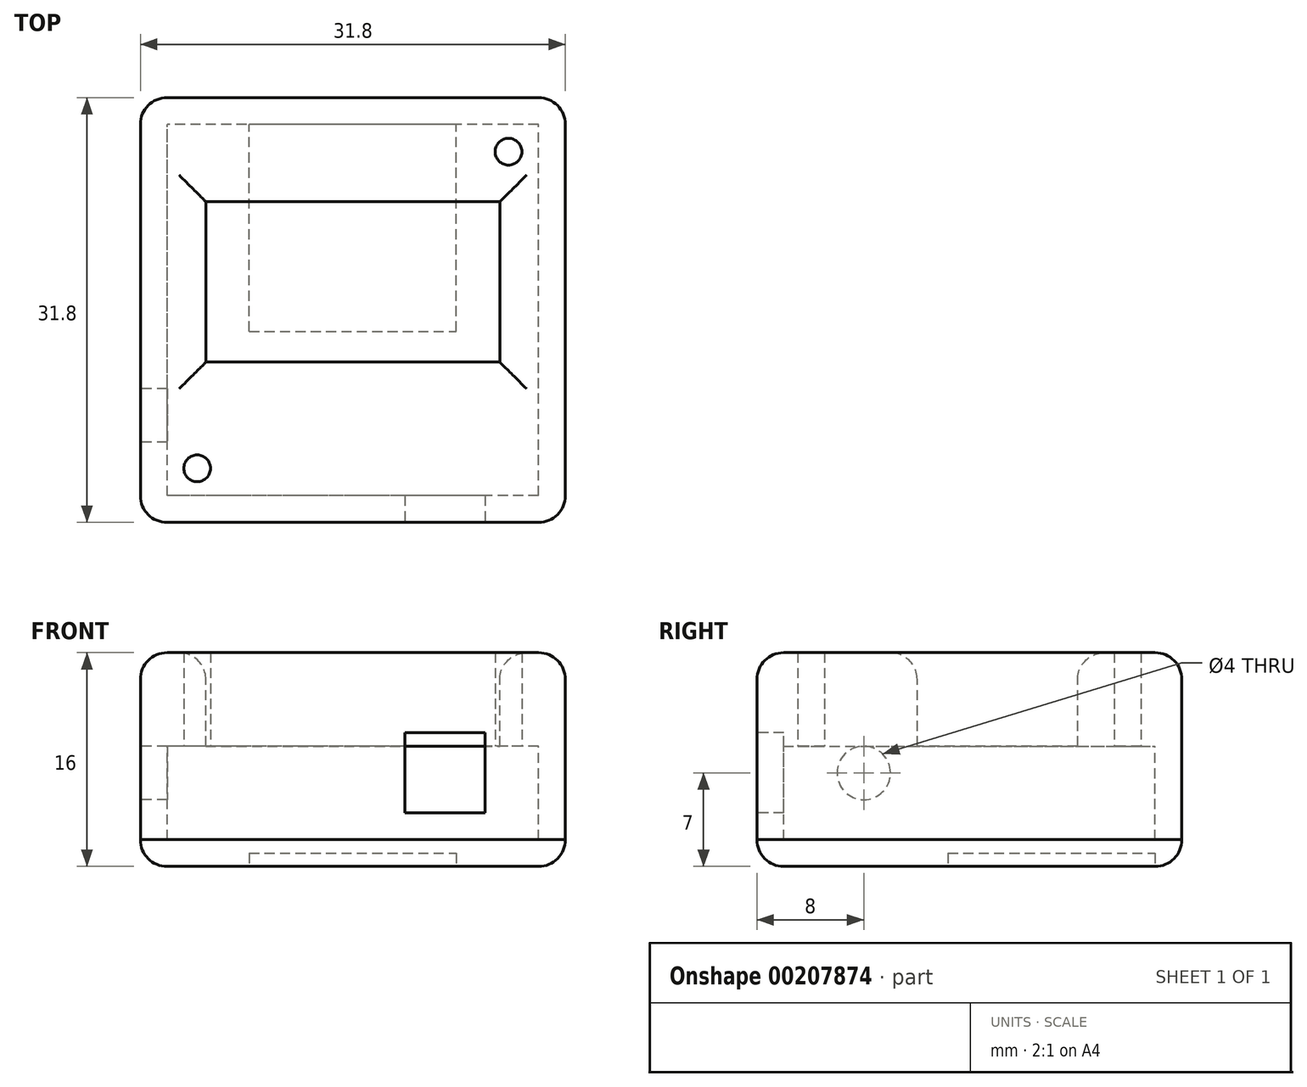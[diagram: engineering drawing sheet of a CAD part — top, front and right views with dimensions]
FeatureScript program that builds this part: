
annotation { "Feature Type Name" : "Feature", "Feature Type Description" : "" }
export const myFeature = defineFeature(function(context is Context, id is Id, definition is map)
    precondition{}
    {
        {
            var Q0;
            Q0=qCreatedBy(makeId("Top.planeOp"),FACE);
            var sketch = newSketch(context, id + "F0", { "sketchPlane" : qUnion([Q0])});
            skLineSegment(sketch, "E0.bottom", {"start": v(13.9, -13.9) * mm, "end": v(-13.9, -13.9) * mm});
            skLineSegment(sketch, "E0.top", {"start": v(13.9, 13.9) * mm, "end": v(-13.9, 13.9) * mm});
            skLineSegment(sketch, "E0.left", {"start": v(13.9, -13.9) * mm, "end": v(13.9, 13.9) * mm});
            skLineSegment(sketch, "E0.right", {"start": v(-13.9, -13.9) * mm, "end": v(-13.9, 13.9) * mm});
            skPoint(sketch, "E0.middle", {"position": v(0, 0) * mm});
            skCircle(sketch, "E1", {"center": v(-11.65, 11.85) * mm, "radius": 1 * mm});
            skLineSegment(sketch, "E2", {"start": v(0, 0) * mm, "end": v(0, 13.9) * mm, "construction": true});
            skCircle(sketch, "E3.MirrorC", {"center": v(11.65, 11.85) * mm, "radius": 1 * mm});
            skLineSegment(sketch, "E4", {"start": v(0, 0) * mm, "end": v(13.9, 0) * mm, "construction": true});
            skCircle(sketch, "E5.MirrorC", {"center": v(-11.65, -11.85) * mm, "radius": 1 * mm});
            skCircle(sketch, "E6.MirrorC", {"center": v(11.65, -11.85) * mm, "radius": 1 * mm});
            skLineSegment(sketch, "E7.bottom", {"start": v(-11, 8.1) * mm, "end": v(11, 8.1) * mm});
            skLineSegment(sketch, "E7.top", {"start": v(-11, -3.9) * mm, "end": v(11, -3.9) * mm});
            skLineSegment(sketch, "E7.left", {"start": v(-11, 8.1) * mm, "end": v(-11, -3.9) * mm});
            skLineSegment(sketch, "E7.right", {"start": v(11, 8.1) * mm, "end": v(11, -3.9) * mm});
            skPoint(sketch, "E8", {"position": v(0, 8.1) * mm});
            skLineSegment(sketch, "E9.0", {"start": v(15.9, -13.9) * mm, "end": v(15.9, 13.9) * mm});
            skLineSegment(sketch, "E9.1", {"start": v(13.9, -15.9) * mm, "end": v(-13.9, -15.9) * mm});
            skLineSegment(sketch, "E9.2", {"start": v(-15.9, -13.9) * mm, "end": v(-15.9, 13.9) * mm});
            skLineSegment(sketch, "E9.3", {"start": v(13.9, 15.9) * mm, "end": v(-13.9, 15.9) * mm});
            skPoint(sketch, "E10.visualSharp", {"position": v(-15.9, 15.9) * mm});
            skArc(sketch, "E10.filletArc", {"start": v(-13.9, 15.9) * mm, "mid": v(-15.31, 15.31) * mm, "end": v(-15.9, 13.9) * mm});
            skPoint(sketch, "E11.visualSharp", {"position": v(15.9, 15.9) * mm});
            skArc(sketch, "E11.filletArc", {"start": v(15.9, 13.9) * mm, "mid": v(15.31, 15.31) * mm, "end": v(13.9, 15.9) * mm});
            skPoint(sketch, "E12.visualSharp", {"position": v(15.9, -15.9) * mm});
            skArc(sketch, "E12.filletArc", {"start": v(13.9, -15.9) * mm, "mid": v(15.31, -15.31) * mm, "end": v(15.9, -13.9) * mm});
            skPoint(sketch, "E13.visualSharp", {"position": v(-15.9, -15.9) * mm});
            skArc(sketch, "E13.filletArc", {"start": v(-15.9, -13.9) * mm, "mid": v(-15.31, -15.31) * mm, "end": v(-13.9, -15.9) * mm});
            skSolve(sketch);
        }
        {
            var Q0;
            Q0=makeQuery(id+"F0.imprint","IMPRINT",FACE,{"disambiguationData":[TD([[makeQuery(id+"F0.imprint","IMPRINT",EDGE,{"derivedFrom":sQuery(id+"F0.wireOp",EDGE,"E0.bottom")}),1.0]])]});
            var Q1;
            Q1=makeQuery(id+"F0.imprint","IMPRINT",FACE,{"disambiguationData":[TD([[makeQuery(id+"F0.imprint","IMPRINT",EDGE,{"derivedFrom":sQuery(id+"F0.wireOp",EDGE,"E0.bottom")}),-1.0]])]});
            var Q2;
            Q2=makeQuery(id+"F0.imprint","IMPRINT",FACE,{"disambiguationData":[TD([[makeQuery(id+"F0.imprint","IMPRINT",EDGE,{"derivedFrom":sQuery(id+"F0.wireOp",EDGE,"E5.MirrorC")}),-1.0]])]});
            var Q3;
            Q3=makeQuery(id+"F0.imprint","IMPRINT",FACE,{"disambiguationData":[TD([[makeQuery(id+"F0.imprint","IMPRINT",EDGE,{"derivedFrom":sQuery(id+"F0.wireOp",EDGE,"E6.MirrorC")}),1.0]])]});
            var Q4;
            Q4=makeQuery(id+"F0.imprint","IMPRINT",FACE,{"disambiguationData":[TD([[makeQuery(id+"F0.imprint","IMPRINT",EDGE,{"derivedFrom":sQuery(id+"F0.wireOp",EDGE,"E3.MirrorC")}),-1.0]])]});
            var Q5;
            Q5=makeQuery(id+"F0.imprint","IMPRINT",FACE,{"disambiguationData":[TD([[makeQuery(id+"F0.imprint","IMPRINT",EDGE,{"derivedFrom":sQuery(id+"F0.wireOp",EDGE,"E1")}),1.0]])]});
            extrude(context, id + "F1", {"entities" : qUnion([Q0, Q1, Q2, Q3, Q4, Q5]), "depth" : 2 * mm});
        }
        {
            var Q0;
            Q0=makeQuery(id+"F1.opExtrude","CAP_EDGE",EDGE,{"disambiguationData":[OSD([sQuery(id+"F0.wireOp",EDGE,"E7.bottom")])],"isStart":false});
            var Q1;
            Q1=makeQuery(id+"F1.opExtrude","CAP_EDGE",EDGE,{"disambiguationData":[OSD([sQuery(id+"F0.wireOp",EDGE,"E7.left")])],"isStart":false});
            var Q2;
            Q2=makeQuery(id+"F1.opExtrude","CAP_EDGE",EDGE,{"disambiguationData":[OSD([sQuery(id+"F0.wireOp",EDGE,"E7.right")])],"isStart":false});
            var Q3;
            Q3=makeQuery(id+"F1.opExtrude","CAP_EDGE",EDGE,{"disambiguationData":[OSD([sQuery(id+"F0.wireOp",EDGE,"E7.top")])],"isStart":false});
            var Q4;
            Q4=makeQuery(id+"F1.opExtrude","CAP_EDGE",EDGE,{"disambiguationData":[OSD([sQuery(id+"F0.wireOp",EDGE,"E9.2")])],"isStart":false});
            fillet(context, id + "F2", {"entities" : qUnion([Q0, Q1, Q2, Q3, Q4]), "radius" : 2 * mm, "tangentPropagation" : true, "allowEdgeOverflow" : false});
        }
        {
            var Q0;
            Q0=makeQuery(id+"F0.imprint","IMPRINT",FACE,{"disambiguationData":[TD([[makeQuery(id+"F0.imprint","IMPRINT",EDGE,{"derivedFrom":sQuery(id+"F0.wireOp",EDGE,"E0.bottom")}),1.0]])]});
            extrude(context, id + "F3", {"entities" : qUnion([Q0]), "operationType" : NewBodyOperationType.ADD, "oppositeDirection" : true, "depth" : 12 * mm});
        }
        {
            var Q0;
            Q0=makeQuery(id+"F3.opExtrude","CAP_FACE",FACE,{"disambiguationData":[OSD([sQuery(id+"F0.wireOp",EDGE,"E0.bottom"),sQuery(id+"F0.wireOp",EDGE,"E0.top"),sQuery(id+"F0.wireOp",EDGE,"E0.left"),sQuery(id+"F0.wireOp",EDGE,"E0.right"),sQuery(id+"F0.wireOp",EDGE,"E9.0"),sQuery(id+"F0.wireOp",EDGE,"E9.1"),sQuery(id+"F0.wireOp",EDGE,"E9.2"),sQuery(id+"F0.wireOp",EDGE,"E9.3"),sQuery(id+"F0.wireOp",EDGE,"E10.filletArc"),sQuery(id+"F0.wireOp",EDGE,"E11.filletArc"),sQuery(id+"F0.wireOp",EDGE,"E12.filletArc"),sQuery(id+"F0.wireOp",EDGE,"E13.filletArc")])],"isStart":false});
            var sketch = newSketch(context, id + "F4", { "sketchPlane" : qUnion([Q0])});
            skLineSegment(sketch, "E14.0", {"start": v(-15.9, 13.9) * mm, "end": v(-15.9, -13.9) * mm});
            skArc(sketch, "E15.0", {"start": v(-15.9, 13.9) * mm, "mid": v(-15.31, 15.31) * mm, "end": v(-13.9, 15.9) * mm});
            skLineSegment(sketch, "E16.0", {"start": v(13.9, 15.9) * mm, "end": v(-13.9, 15.9) * mm});
            skArc(sketch, "E17.0", {"start": v(13.9, 15.9) * mm, "mid": v(15.31, 15.31) * mm, "end": v(15.9, 13.9) * mm});
            skLineSegment(sketch, "E18.0", {"start": v(15.9, 13.9) * mm, "end": v(15.9, -13.9) * mm});
            skArc(sketch, "E19.0", {"start": v(15.9, -13.9) * mm, "mid": v(15.31, -15.31) * mm, "end": v(13.9, -15.9) * mm});
            skLineSegment(sketch, "E20.0", {"start": v(13.9, -15.9) * mm, "end": v(-13.9, -15.9) * mm});
            skArc(sketch, "E21.0", {"start": v(-13.9, -15.9) * mm, "mid": v(-15.31, -15.31) * mm, "end": v(-15.9, -13.9) * mm});
            skSolve(sketch);
        }
        {
            var Q0;
            Q0=makeQuery(id+"F4.imprint","IMPRINT",FACE,{"disambiguationData":[TD([[makeQuery(id+"F4.imprint","IMPRINT",EDGE,{"derivedFrom":makeQuery(id+"F3.opExtrude","CAP_EDGE",EDGE,{"disambiguationData":[OSD([sQuery(id+"F0.wireOp",EDGE,"E0.bottom")])],"isStart":false})}),1.0]])]});
            var Q1;
            Q1=makeQuery(id+"F4.imprint","IMPRINT",FACE,{"disambiguationData":[TD([[makeQuery(id+"F4.imprint","IMPRINT",EDGE,{"derivedFrom":sQuery(id+"F4.wireOp",EDGE,"E14.0")}),1.0]])]});
            extrude(context, id + "F5", {"entities" : qUnion([Q0, Q1]), "depth" : 2 * mm});
        }
        {
            var Q0;
            Q0=makeQuery(id+"F1.opExtrude","SWEPT_BODY",BODY,{"disambiguationData":[OSD([sQuery(id+"F0.wireOp",EDGE,"E7.bottom"),sQuery(id+"F0.wireOp",EDGE,"E7.top"),sQuery(id+"F0.wireOp",EDGE,"E7.left"),sQuery(id+"F0.wireOp",EDGE,"E7.right"),sQuery(id+"F0.wireOp",EDGE,"E9.0"),sQuery(id+"F0.wireOp",EDGE,"E9.1"),sQuery(id+"F0.wireOp",EDGE,"E9.2"),sQuery(id+"F0.wireOp",EDGE,"E9.3"),sQuery(id+"F0.wireOp",EDGE,"E10.filletArc"),sQuery(id+"F0.wireOp",EDGE,"E11.filletArc"),sQuery(id+"F0.wireOp",EDGE,"E12.filletArc"),sQuery(id+"F0.wireOp",EDGE,"E13.filletArc")])]});
            var Q1;
            Q1=makeQuery(id+"F5.opExtrude","SWEPT_BODY",BODY,{"disambiguationData":[OSD([sQuery(id+"F4.wireOp",EDGE,"E14.0"),sQuery(id+"F4.wireOp",EDGE,"E15.0"),sQuery(id+"F4.wireOp",EDGE,"E16.0"),sQuery(id+"F4.wireOp",EDGE,"E17.0"),sQuery(id+"F4.wireOp",EDGE,"E18.0"),sQuery(id+"F4.wireOp",EDGE,"E19.0"),sQuery(id+"F4.wireOp",EDGE,"E20.0"),sQuery(id+"F4.wireOp",EDGE,"E21.0")])]});
            booleanBodies(context, id + "F6", {"operationType" : BooleanOperationType.SUBTRACTION, "tools" : qUnion([Q0]), "targets" : qUnion([Q1]), "keepTools" : true});
        }
        {
            var Q0;
            Q0=makeQuery(id+"F3.opExtrude","SWEPT_FACE",FACE,{"disambiguationData":[OSD([sQuery(id+"F0.wireOp",EDGE,"E9.1")])]});
            var sketch = newSketch(context, id + "F7", { "sketchPlane" : qUnion([Q0])});
            skLineSegment(sketch, "E22.bottom", {"start": v(3.9, -4) * mm, "end": v(9.9, -4) * mm});
            skLineSegment(sketch, "E22.top", {"start": v(3.9, -10) * mm, "end": v(9.9, -10) * mm});
            skLineSegment(sketch, "E22.left", {"start": v(3.9, -4) * mm, "end": v(3.9, -10) * mm});
            skLineSegment(sketch, "E22.right", {"start": v(9.9, -4) * mm, "end": v(9.9, -10) * mm});
            skPoint(sketch, "E23", {"position": v(3.9, -7) * mm});
            skSolve(sketch);
        }
        {
            var Q0;
            Q0=makeQuery(id+"F7.imprint","IMPRINT",FACE,{"disambiguationData":[TD([[makeQuery(id+"F7.imprint","IMPRINT",EDGE,{"derivedFrom":sQuery(id+"F7.wireOp",EDGE,"RuFjycDv-3AOw-nEw2-OPAT-4idIWS5Qx4Iz")}),1.0]])]});
            var Q1;
            Q1=makeQuery(id+"F7.imprint","IMPRINT",FACE,{"disambiguationData":[TD([[makeQuery(id+"F7.imprint","IMPRINT",EDGE,{"derivedFrom":sQuery(id+"F7.wireOp",EDGE,"E22.bottom")}),-1.0]])]});
            extrude(context, id + "F8", {"entities" : qUnion([Q0, Q1]), "operationType" : NewBodyOperationType.REMOVE, "oppositeDirection" : true, "depth" : 5 * mm});
        }
        {
            var Q0;
            Q0=makeQuery(id+"F3.opExtrude","SWEPT_FACE",FACE,{"disambiguationData":[OSD([sQuery(id+"F0.wireOp",EDGE,"E9.2")])]});
            var sketch = newSketch(context, id + "F9", { "sketchPlane" : qUnion([Q0])});
            skPoint(sketch, "E24.0", {"position": v(15.9, -7) * mm});
            skCircle(sketch, "E25", {"center": v(7.9, -7) * mm, "radius": 2 * mm});
            skSolve(sketch);
        }
        {
            var Q0;
            Q0=makeQuery(id+"F9.imprint","IMPRINT",FACE,{"disambiguationData":[TD([[makeQuery(id+"F9.imprint","IMPRINT",EDGE,{"derivedFrom":sQuery(id+"F9.wireOp",EDGE,"E25")}),1.0]])]});
            extrude(context, id + "F10", {"entities" : qUnion([Q0]), "operationType" : NewBodyOperationType.REMOVE, "oppositeDirection" : true, "depth" : 5 * mm});
        }
        {
            var Q0;
            Q0=makeQuery(id+"F0.imprint","IMPRINT",FACE,{"disambiguationData":[TD([[makeQuery(id+"F0.imprint","IMPRINT",EDGE,{"derivedFrom":sQuery(id+"F0.wireOp",EDGE,"E5.MirrorC")}),-1.0]])]});
            var Q1;
            Q1=makeQuery(id+"F0.imprint","IMPRINT",FACE,{"disambiguationData":[TD([[makeQuery(id+"F0.imprint","IMPRINT",EDGE,{"derivedFrom":sQuery(id+"F0.wireOp",EDGE,"E6.MirrorC")}),1.0]])]});
            var Q2;
            Q2=makeQuery(id+"F0.imprint","IMPRINT",FACE,{"disambiguationData":[TD([[makeQuery(id+"F0.imprint","IMPRINT",EDGE,{"derivedFrom":sQuery(id+"F0.wireOp",EDGE,"E1")}),1.0]])]});
            var Q3;
            Q3=makeQuery(id+"F0.imprint","IMPRINT",FACE,{"disambiguationData":[TD([[makeQuery(id+"F0.imprint","IMPRINT",EDGE,{"derivedFrom":sQuery(id+"F0.wireOp",EDGE,"E3.MirrorC")}),-1.0]])]});
            var Q4;
            Q4=sQuery(id+"F0.wireOp",EDGE,"E5.MirrorC");
            var Q5;
            Q5=sQuery(id+"F0.wireOp",EDGE,"E6.MirrorC");
            var Q6;
            Q6=sQuery(id+"F0.wireOp",EDGE,"E1");
            var Q7;
            Q7=sQuery(id+"F0.wireOp",EDGE,"E3.MirrorC");
            extrude(context, id + "F11", {"entities" : qUnion([Q0, Q1, Q2, Q3]), "operationType" : NewBodyOperationType.ADD, "surfaceEntities" : qUnion([Q4, Q5, Q6, Q7]), "oppositeDirection" : true, "depth" : 5 * mm});
        }
        {
            var Q0;
            Q0=makeQuery(id+"F5.opExtrude","CAP_EDGE",EDGE,{"disambiguationData":[OSD([sQuery(id+"F4.wireOp",EDGE,"E16.0")])],"isStart":false});
            fillet(context, id + "F12", {"entities" : qUnion([Q0]), "radius" : 2 * mm, "tangentPropagation" : true, "allowEdgeOverflow" : false});
        }
        {
            var Q0;
            Q0=makeQuery(id+"F5.opExtrude","CAP_FACE",FACE,{"disambiguationData":[OSD([sQuery(id+"F4.wireOp",EDGE,"E14.0"),sQuery(id+"F4.wireOp",EDGE,"E15.0"),sQuery(id+"F4.wireOp",EDGE,"E16.0"),sQuery(id+"F4.wireOp",EDGE,"E17.0"),sQuery(id+"F4.wireOp",EDGE,"E18.0"),sQuery(id+"F4.wireOp",EDGE,"E19.0"),sQuery(id+"F4.wireOp",EDGE,"E20.0"),sQuery(id+"F4.wireOp",EDGE,"E21.0")])],"isStart":false});
            var sketch = newSketch(context, id + "F13", { "sketchPlane" : qUnion([Q0])});
            skLineSegment(sketch, "E26.bottom", {"start": v(-7.75, 1.6) * mm, "end": v(7.75, 1.6) * mm});
            skLineSegment(sketch, "E26.top", {"start": v(-7.75, -13.9) * mm, "end": v(7.75, -13.9) * mm});
            skLineSegment(sketch, "E26.left", {"start": v(-7.75, 1.6) * mm, "end": v(-7.75, -13.9) * mm});
            skLineSegment(sketch, "E26.right", {"start": v(7.75, 1.6) * mm, "end": v(7.75, -13.9) * mm});
            skPoint(sketch, "E27", {"position": v(0, -13.9) * mm});
            skSolve(sketch);
        }
        {
            var Q0;
            Q0=makeQuery(id+"F13.imprint","IMPRINT",FACE,{"disambiguationData":[TD([[makeQuery(id+"F13.imprint","IMPRINT",EDGE,{"derivedFrom":sQuery(id+"F13.wireOp",EDGE,"E26.bottom")}),-1.0]])]});
            extrude(context, id + "F14", {"entities" : qUnion([Q0]), "operationType" : NewBodyOperationType.REMOVE, "oppositeDirection" : true, "depth" : 1 * mm});
        }
    });
